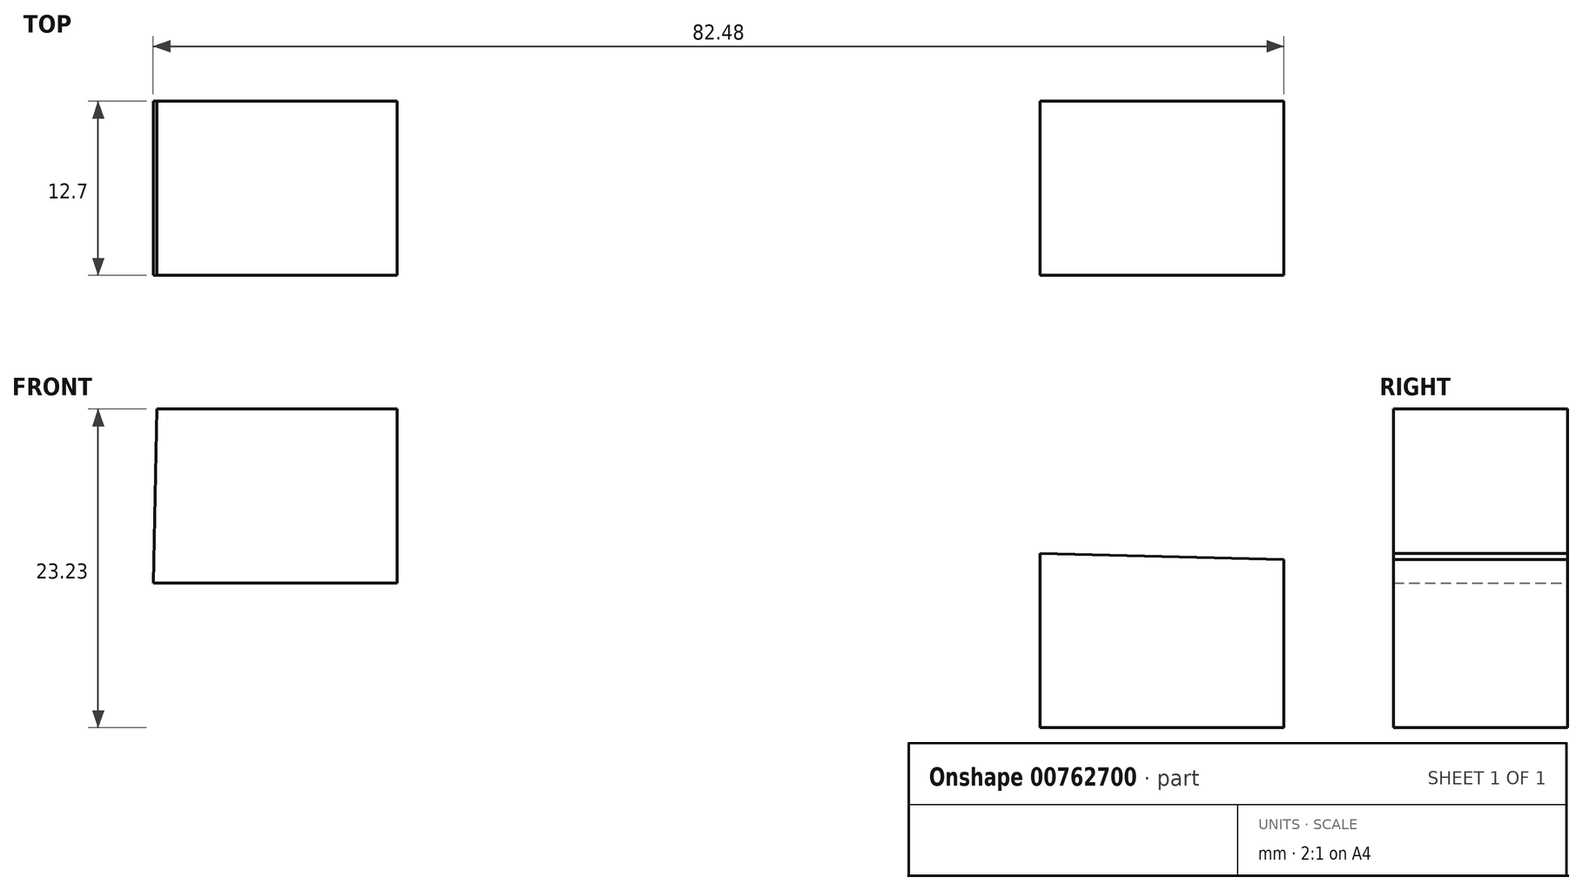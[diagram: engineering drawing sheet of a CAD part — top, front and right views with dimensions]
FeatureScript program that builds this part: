
annotation { "Feature Type Name" : "Feature", "Feature Type Description" : "" }
export const myFeature = defineFeature(function(context is Context, id is Id, definition is map)
    precondition{}
    {
        {
            var Q0;
            Q0=qCreatedBy(makeId("Front.planeOp"),FACE);
            var sketch = newSketch(context, id + "F0", { "sketchPlane" : qUnion([Q0])});
            skLineSegment(sketch, "E0", {"start": v(-31.45, 23.54) * mm, "end": v(-13.67, 23.54) * mm});
            skLineSegment(sketch, "E1", {"start": v(-13.67, 23.54) * mm, "end": v(-13.67, 36.23) * mm});
            skLineSegment(sketch, "E2", {"start": v(-13.67, 36.23) * mm, "end": v(-31.18, 36.23) * mm});
            skLineSegment(sketch, "E3", {"start": v(-31.18, 36.23) * mm, "end": v(-31.45, 23.54) * mm});
            skLineSegment(sketch, "E4", {"start": v(-31.31, 29.89) * mm, "end": v(-39.48, 30.06) * mm});
            skLineSegment(sketch, "E5", {"start": v(-39.48, 30.06) * mm, "end": v(-39.48, 20.73) * mm});
            skLineSegment(sketch, "E6", {"start": v(-39.48, 20.73) * mm, "end": v(-48.3, 20.91) * mm});
            skSolve(sketch);
        }
        {
            var Q0;
            Q0=qCreatedBy(makeId("Front.planeOp"),FACE);
            var sketch = newSketch(context, id + "F1", { "sketchPlane" : qUnion([Q0])});
            skLineSegment(sketch, "E7", {"start": v(33.25, 25.7) * mm, "end": v(33.25, 13) * mm});
            skLineSegment(sketch, "E8", {"start": v(33.25, 13) * mm, "end": v(51.03, 13) * mm});
            skLineSegment(sketch, "E9", {"start": v(51.03, 13) * mm, "end": v(51.03, 25.27) * mm});
            skLineSegment(sketch, "E10", {"start": v(51.03, 25.27) * mm, "end": v(33.25, 25.7) * mm});
            skLineSegment(sketch, "E11", {"start": v(51.03, 19.14) * mm, "end": v(59.28, 19.14) * mm});
            skLineSegment(sketch, "E12", {"start": v(59.28, 19.14) * mm, "end": v(59.28, 9.75) * mm});
            skLineSegment(sketch, "E13", {"start": v(59.28, 9.75) * mm, "end": v(67.51, 9.75) * mm});
            skSolve(sketch);
        }
        {
            var Q0;
            {var subQ3=sQuery(id+"F0.wireOp",EDGE,"E0");Q0=makeQuery(id+"F0.imprint","IMPRINT",FACE,{"disambiguationData":[TD([[makeQuery(id+"F0.imprint","IMPRINT",EDGE,{"derivedFrom":subQ3}),1.0]])]});}
            var Q1;
            Q1=makeQuery(id+"F1.imprint","IMPRINT",FACE,{"disambiguationData":[TD([[makeQuery(id+"F1.imprint","IMPRINT",EDGE,{"derivedFrom":sQuery(id+"F1.wireOp",EDGE,"E7")}),1.0]])]});
            extrude(context, id + "F2", {"entities" : qUnion([Q0, Q1]), "depth" : 12.7 * mm, "offsetDistance" : 25.4 * mm});
        }
    });
